# Revit family: 63_UN_Lightline_Coreline Tubular WT210C PC_Signify
name_source: partatom
category: Lighting Fixtures
units: mm (PartAtom-declared; Revit-internal decimal feet)

## family parameters
Always vertical = No
Cut with Voids When Loaded = No
Light Source = Yes
OmniClass Number = 23.80.70.11.14.11
OmniClass Title = Downlights
Part Type = Normal
Room Calculation Point = Yes
Round Connector Dimension = Use Diameter
Shared = No
Work Plane-Based = No

## types (2) — shared parameters
Assembly Code = 63.0
Color Filter = 16777215
Dimming Lamp Color Temperature Shift = <None>
IfcExportAs = IfcLightFixtureType
IfcExportType = USERDEFINED
Lamp = LED
Manufacturer = Signify
Model = Coreline Tubular Waterproof
Tilt Angle = 90.00°
Type Comments = WT210PC
URL = https://www.signify.com
Voltage = 230 V

## per-type parameters (varying)
| type | Apparent Load | Emit from Line Length | Length | Photometric Web File | Wattage Comments |
| WT210C LED50S_840 PC PSU L1200 | 39 VA | 1156 mm | 1211 mm  [stored 3.9731 ft] | WT210C LED50S_840 PC PSU L1200.ies | 39 W |
| WT210C LED70S_840 PC PSU L1500 | 54 VA | 1456 mm | 1511 mm | WT210C LED70S_840 PC PSU L1500.ies | 54 W |

note: [stored X ft] marks values corroborated as IEEE doubles in the binary element streams (Revit-internal decimal feet)

## geometry (parser evidence)
native form markers: Sweep x3
no freeform markers — native parametric forms only
